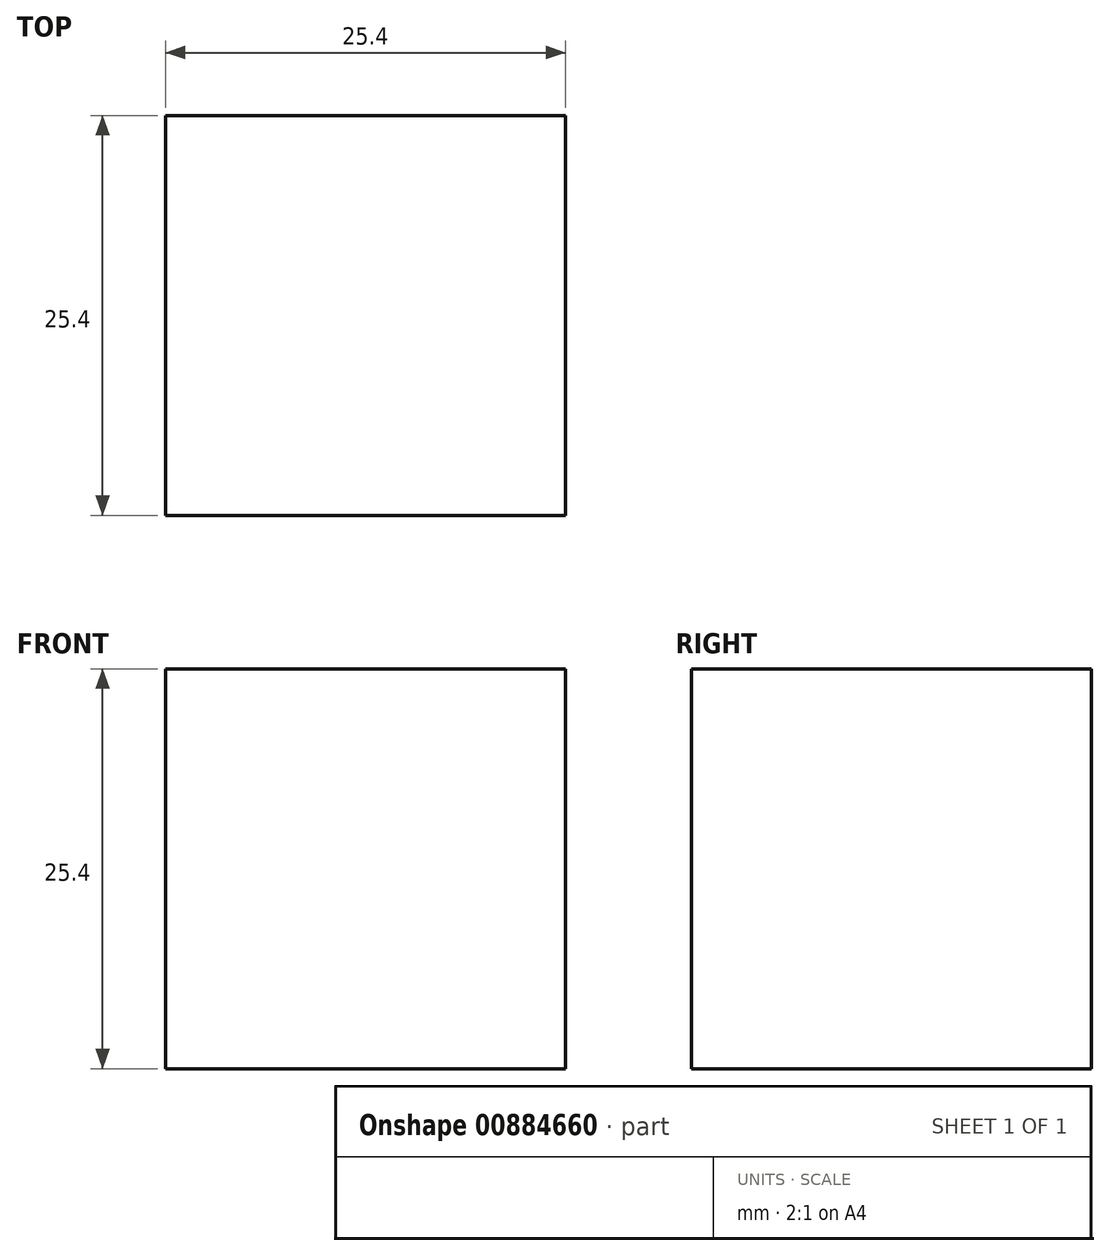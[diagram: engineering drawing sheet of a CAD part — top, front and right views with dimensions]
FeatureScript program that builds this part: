
annotation { "Feature Type Name" : "Feature", "Feature Type Description" : "" }
export const myFeature = defineFeature(function(context is Context, id is Id, definition is map)
    precondition{}
    {
        {
            var Q0;
            Q0=qCreatedBy(makeId("Front.planeOp"),FACE);
            var sketch = newSketch(context, id + "F0", { "sketchPlane" : qUnion([Q0])});
            skLineSegment(sketch, "E0.bottom", {"start": v(-7.72, 5.3) * mm, "end": v(17.68, 5.3) * mm});
            skLineSegment(sketch, "E0.top", {"start": v(-7.72, -20.1) * mm, "end": v(17.68, -20.1) * mm});
            skLineSegment(sketch, "E0.left", {"start": v(-7.72, 5.3) * mm, "end": v(-7.72, -20.1) * mm});
            skLineSegment(sketch, "E0.right", {"start": v(17.68, 5.3) * mm, "end": v(17.68, -20.1) * mm});
            skSolve(sketch);
        }
        {
            var Q0;
            Q0 = qSketchRegion(id + "F0", true);
            extrude(context, id + "F1", {"entities" : qUnion([Q0]), "depth" : 25.4 * mm, "offsetDistance" : 25.4 * mm});
        }
    });
